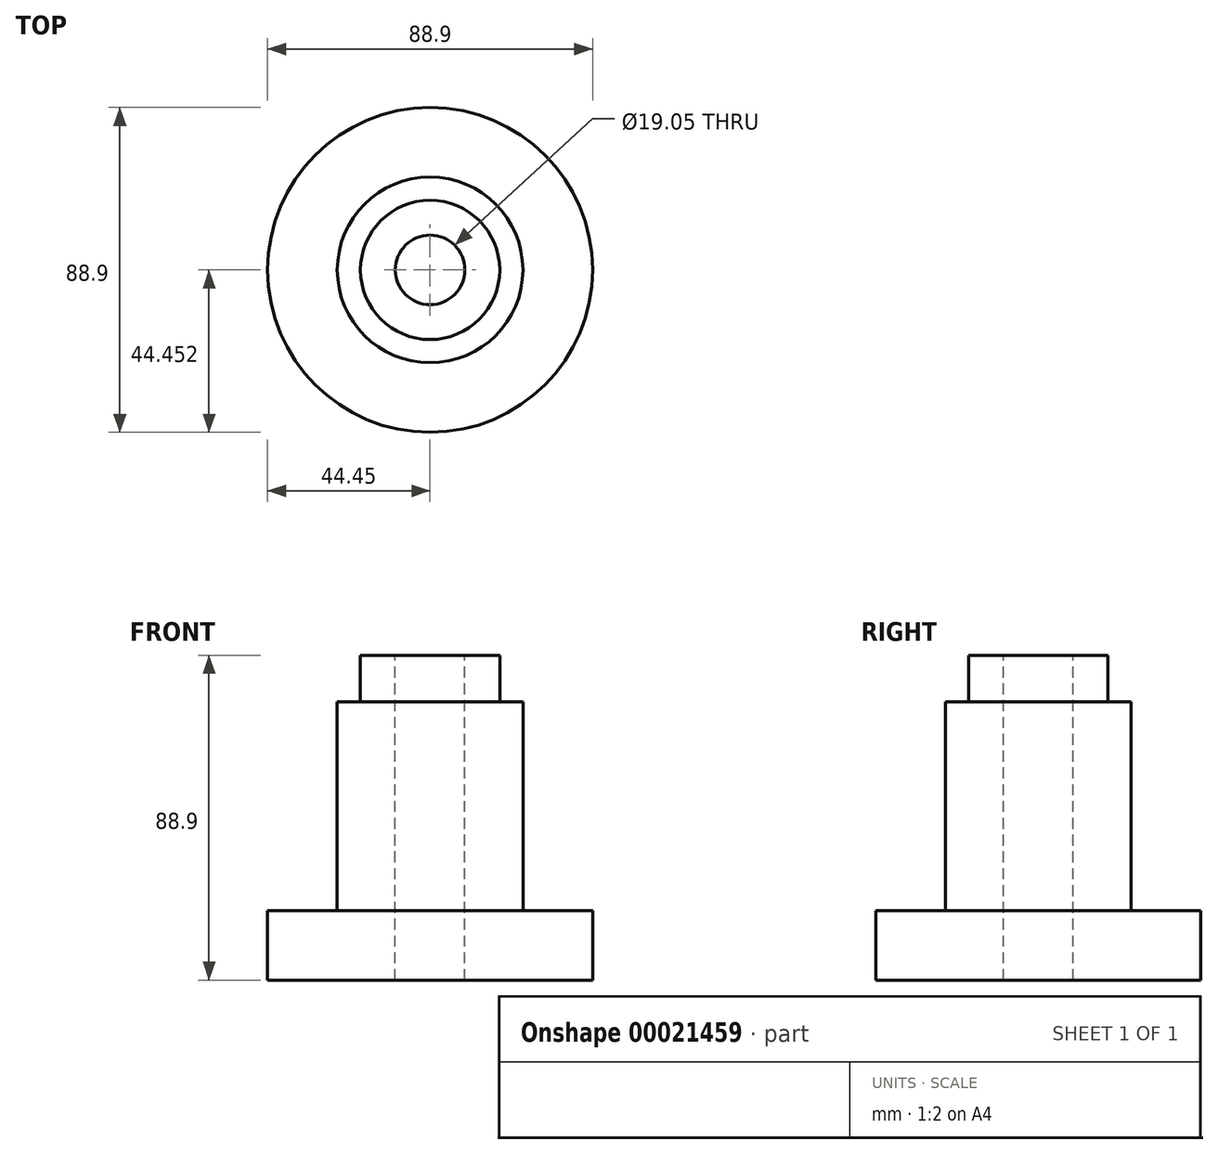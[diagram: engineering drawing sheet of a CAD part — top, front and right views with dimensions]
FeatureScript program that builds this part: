
annotation { "Feature Type Name" : "Feature", "Feature Type Description" : "" }
export const myFeature = defineFeature(function(context is Context, id is Id, definition is map)
    precondition{}
    {
        {
            var Q0;
            Q0=qCreatedBy(makeId("Right.planeOp"),FACE);
            var sketch = newSketch(context, id + "F0", { "sketchPlane" : qUnion([Q0])});
            skLineSegment(sketch, "E0.bottom", {"start": v(-27.35, 40.68) * mm, "end": v(-17.83, 40.68) * mm});
            skLineSegment(sketch, "E0.top", {"start": v(-27.35, -48.22) * mm, "end": v(-17.83, -48.22) * mm});
            skLineSegment(sketch, "E0.left", {"start": v(-27.35, 40.68) * mm, "end": v(-27.35, -48.22) * mm});
            skLineSegment(sketch, "E0.right", {"start": v(-17.83, 40.68) * mm, "end": v(-17.83, -48.22) * mm});
            skLineSegment(sketch, "E1.bottom", {"start": v(-27.35, 40.68) * mm, "end": v(-36.88, 40.68) * mm});
            skLineSegment(sketch, "E1.top", {"start": v(-27.35, -48.22) * mm, "end": v(-36.88, -48.22) * mm});
            skLineSegment(sketch, "E1.right", {"start": v(-36.88, 40.68) * mm, "end": v(-36.88, -48.22) * mm});
            skLineSegment(sketch, "E2.bottom", {"start": v(-17.83, -48.22) * mm, "end": v(-11.48, -48.22) * mm});
            skLineSegment(sketch, "E2.top", {"start": v(-17.83, 27.98) * mm, "end": v(-11.48, 27.98) * mm});
            skLineSegment(sketch, "E2.left", {"start": v(-17.83, -48.22) * mm, "end": v(-17.83, 27.98) * mm});
            skLineSegment(sketch, "E2.right", {"start": v(-11.48, -48.22) * mm, "end": v(-11.48, 27.98) * mm});
            skLineSegment(sketch, "E3.bottom", {"start": v(-11.48, -48.22) * mm, "end": v(7.57, -48.22) * mm});
            skLineSegment(sketch, "E3.top", {"start": v(-11.48, -29.17) * mm, "end": v(7.57, -29.17) * mm});
            skLineSegment(sketch, "E3.left", {"start": v(-11.48, -48.22) * mm, "end": v(-11.48, -29.17) * mm});
            skLineSegment(sketch, "E3.right", {"start": v(7.57, -48.22) * mm, "end": v(7.57, -29.17) * mm});
            skSolve(sketch);
        }
        {
            var Q0;
            Q0=makeQuery(id+"F0.imprint","IMPRINT",FACE,{"disambiguationData":[TD([[makeQuery(id+"F0.imprint","IMPRINT",EDGE,{"derivedFrom":sQuery(id+"F0.wireOp",EDGE,"E0.bottom")}),-1.0]])]});
            var Q1;
            Q1=makeQuery(id+"F0.imprint","IMPRINT",FACE,{"disambiguationData":[TD([[makeQuery(id+"F0.imprint","IMPRINT",EDGE,{"derivedFrom":sQuery(id+"F0.wireOp",EDGE,"E2.bottom")}),1.0]])]});
            var Q2;
            Q2=makeQuery(id+"F0.imprint","IMPRINT",FACE,{"disambiguationData":[TD([[makeQuery(id+"F0.imprint","IMPRINT",EDGE,{"derivedFrom":sQuery(id+"F0.wireOp",EDGE,"E3.bottom")}),1.0]])]});
            var Q3;
            Q3=sQuery(id+"F0.wireOp",EDGE,"E1.right");
            revolve(context, id + "F1", {"entities" : qUnion([Q0, Q1, Q2]), "axis" : qUnion([Q3]), "revolveType" : RevolveType.FULL});
        }
    });
